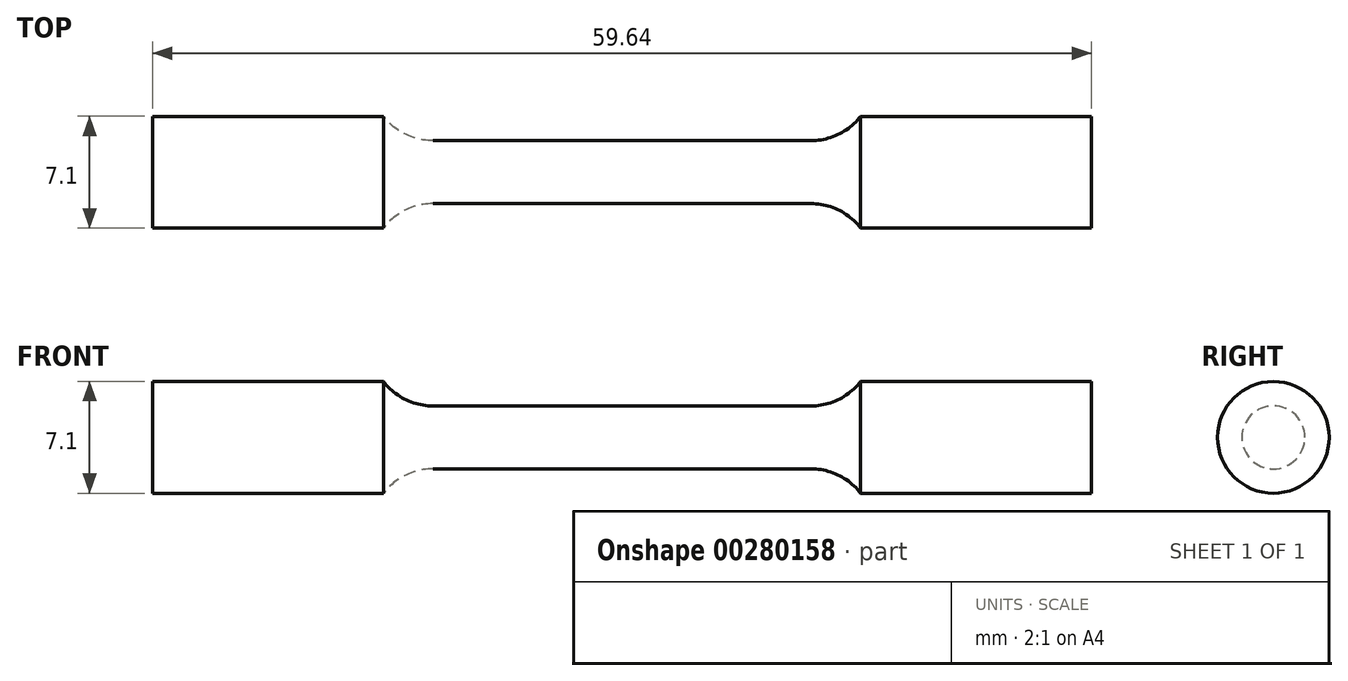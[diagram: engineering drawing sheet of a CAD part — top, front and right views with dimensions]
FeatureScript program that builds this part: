
annotation { "Feature Type Name" : "Feature", "Feature Type Description" : "" }
export const myFeature = defineFeature(function(context is Context, id is Id, definition is map)
    precondition{}
    {
        {
            var Q0;
            Q0=qCreatedBy(makeId("Front.planeOp"),FACE);
            var sketch = newSketch(context, id + "F0", { "sketchPlane" : qUnion([Q0])});
            skLineSegment(sketch, "E0", {"start": v(0, 2) * mm, "end": v(12, 2) * mm});
            skArc(sketch, "E1", {"start": v(12, 2) * mm, "mid": v(13.76, 2.4) * mm, "end": v(15.16, 3.55) * mm});
            skLineSegment(sketch, "E2", {"start": v(15.16, 3.55) * mm, "end": v(29.82, 3.55) * mm});
            skLineSegment(sketch, "E3", {"start": v(29.82, 3.55) * mm, "end": v(29.82, 0) * mm});
            skLineSegment(sketch, "E4.MirrorCS", {"start": v(-29.82, 3.55) * mm, "end": v(-29.82, 0) * mm});
            skLineSegment(sketch, "E5.MirrorCS", {"start": v(-15.16, 3.55) * mm, "end": v(-29.82, 3.55) * mm});
            skLineSegment(sketch, "E6.MirrorCS", {"start": v(0, 2) * mm, "end": v(-12, 2) * mm});
            skArc(sketch, "E7.MirrorCS", {"start": v(-12, 2) * mm, "mid": v(-13.76, 2.4) * mm, "end": v(-15.16, 3.55) * mm});
            skLineSegment(sketch, "E8", {"start": v(-29.82, 0) * mm, "end": v(29.82, 0) * mm});
            skSolve(sketch);
        }
        {
            var Q0;
            Q0 = qSketchRegion(id + "F0", true);
            var Q1;
            Q1=sQuery(id+"F0.wireOp",EDGE,"E8");
            revolve(context, id + "F1", {"entities" : qUnion([Q0]), "axis" : qUnion([Q1]), "revolveType" : RevolveType.FULL});
        }
    });
